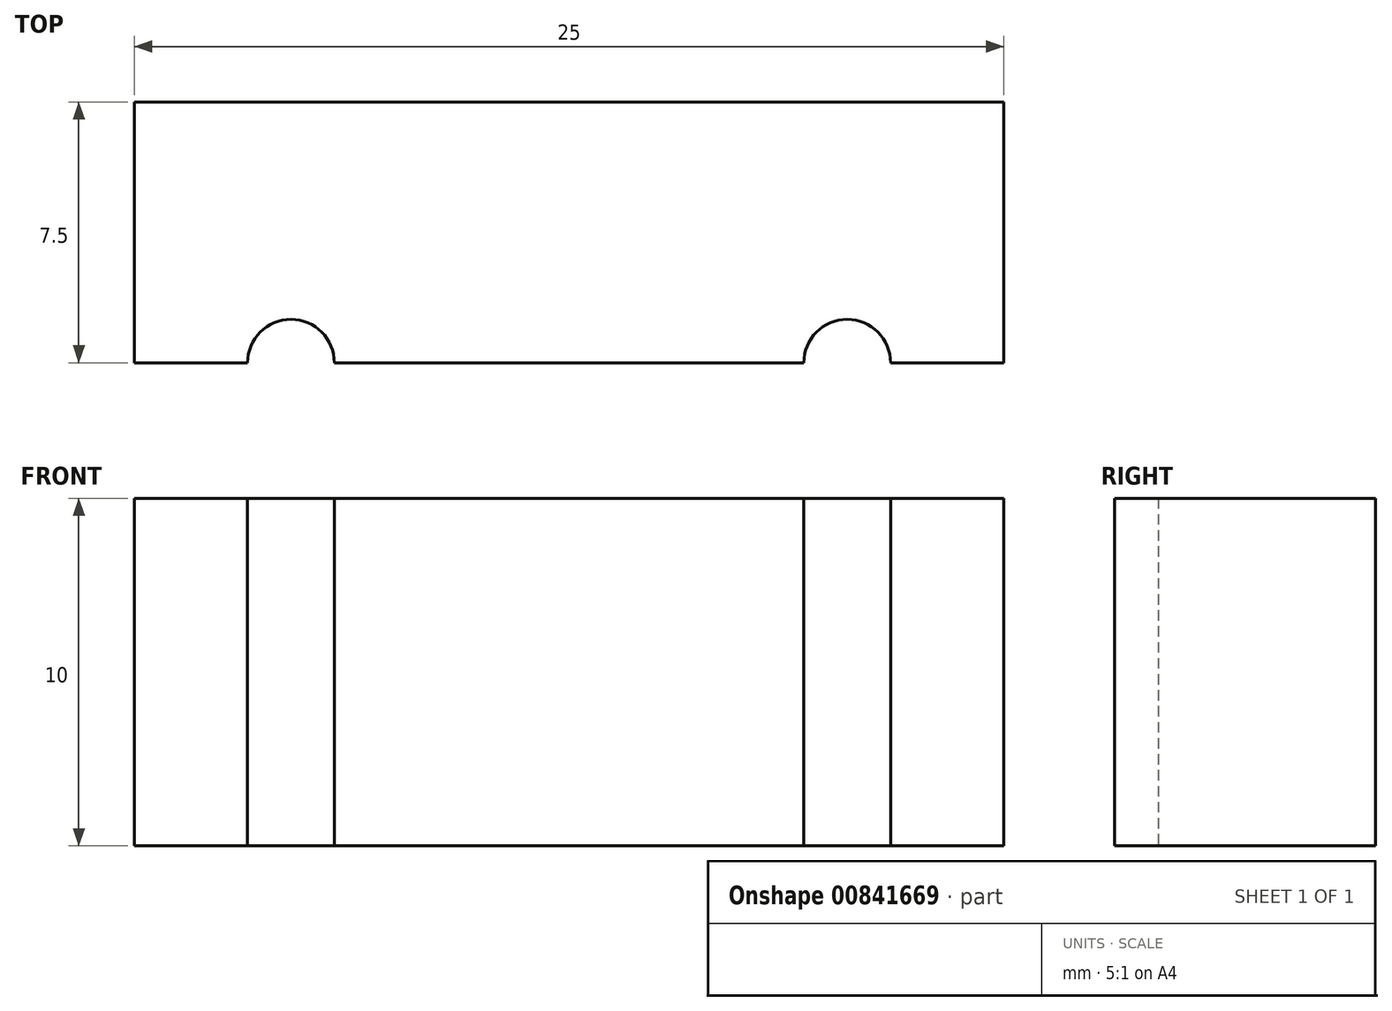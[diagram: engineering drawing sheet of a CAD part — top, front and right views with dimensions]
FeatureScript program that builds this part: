
annotation { "Feature Type Name" : "Feature", "Feature Type Description" : "" }
export const myFeature = defineFeature(function(context is Context, id is Id, definition is map)
    precondition{}
    {
        {
            var Q0;
            Q0=qCreatedBy(makeId("Top.planeOp"),FACE);
            var sketch = newSketch(context, id + "F0", { "sketchPlane" : qUnion([Q0])});
            skLineSegment(sketch, "E0.bottom", {"start": v(-29.6, 13.97) * mm, "end": v(-4.6, 13.97) * mm});
            skLineSegment(sketch, "E0.top", {"start": v(-29.6, -1.03) * mm, "end": v(-4.6, -1.03) * mm});
            skLineSegment(sketch, "E0.left", {"start": v(-29.6, 13.97) * mm, "end": v(-29.6, -1.03) * mm});
            skLineSegment(sketch, "E0.right", {"start": v(-4.6, 13.97) * mm, "end": v(-4.6, -1.03) * mm});
            skLineSegment(sketch, "E1", {"start": v(-29.6, 6.47) * mm, "end": v(-4.6, 6.47) * mm});
            skCircle(sketch, "E2", {"center": v(-25.1, 6.47) * mm, "radius": 1.25 * mm});
            skLineSegment(sketch, "E3", {"start": v(-17.1, 13.97) * mm, "end": v(-17.1, -1.28) * mm});
            skCircle(sketch, "E4.MirrorC", {"center": v(-9.1, 6.47) * mm, "radius": 1.25 * mm});
            skSolve(sketch);
        }
        {
            var Q0;
            Q0=makeQuery(id+"F0.imprint","IMPRINT",FACE,{"disambiguationData":[TD([[makeQuery(id+"F0.imprint","IMPRINT",EDGE,{"derivedFrom":sQuery(id+"F0.wireOp",EDGE,"E0.bottom")}),-1.0]])]});
            extrude(context, id + "F1", {"entities" : qUnion([Q0]), "depth" : 10 * mm, "offsetDistance" : 25.4 * mm});
        }
    });
